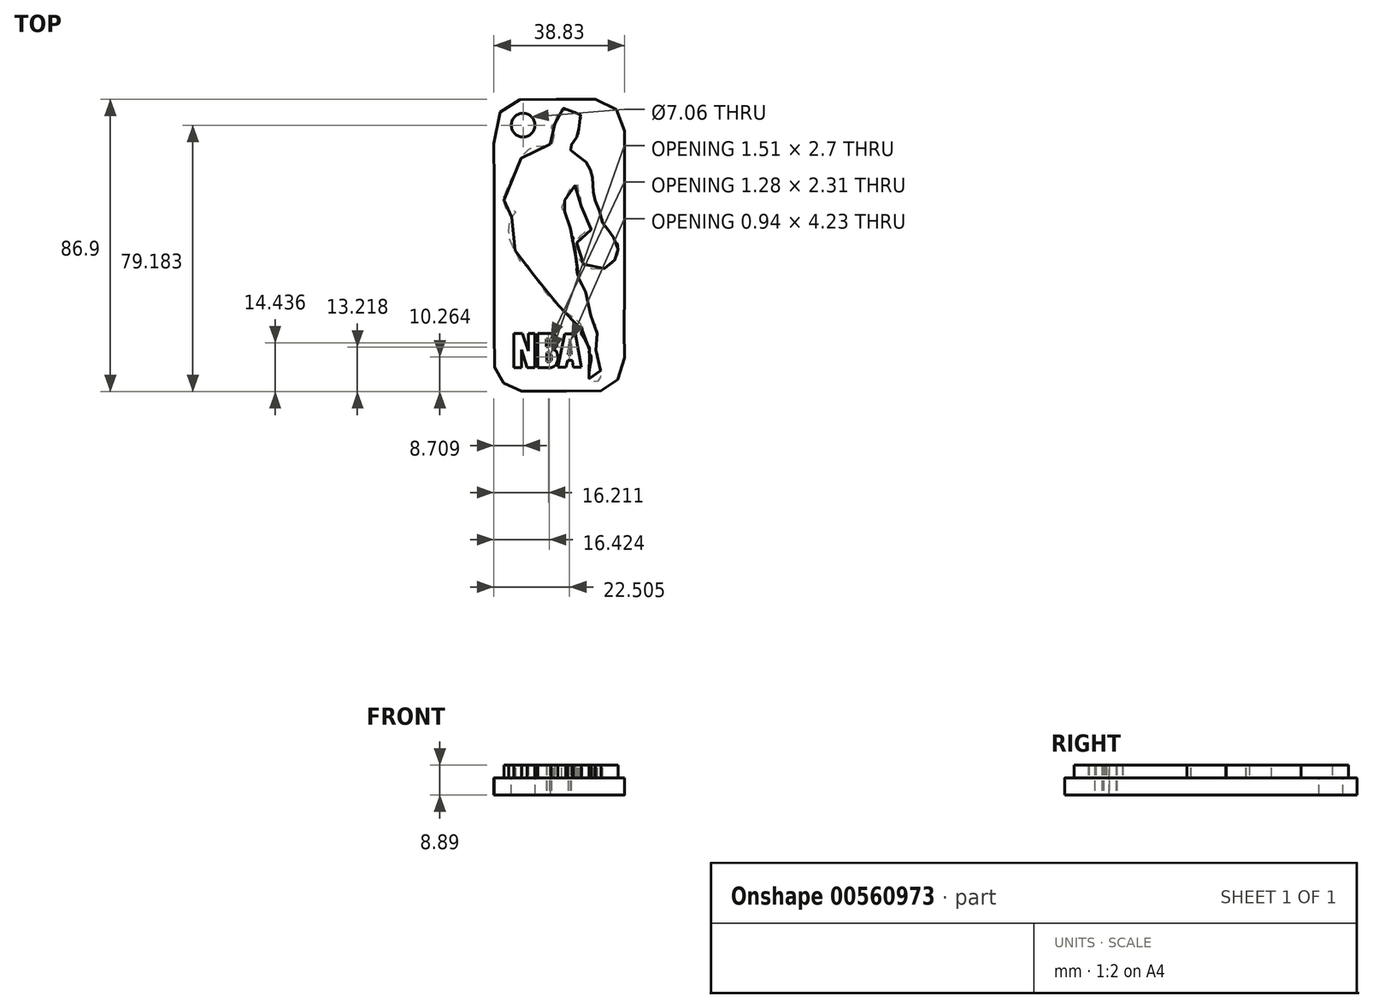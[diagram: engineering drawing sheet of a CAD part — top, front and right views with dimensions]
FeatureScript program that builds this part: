
annotation { "Feature Type Name" : "Feature", "Feature Type Description" : "" }
export const myFeature = defineFeature(function(context is Context, id is Id, definition is map)
    precondition{}
    {
        {
            var Q0;
            Q0=qCreatedBy(makeId("Top.planeOp"),FACE);
            var sketch = newSketch(context, id + "F0", { "sketchPlane" : qUnion([Q0])});
            skFitSpline(sketch, "E0", {"points": [v(-9.33, 40) * mm, v(-11.4, 39.37) * mm, v(-13.37, 38.26) * mm, v(-14.83, 36.7) * mm, v(-16.26, 34.66) * mm, v(-17.02, 30.53) * mm, v(-16.94, 24.3) * mm, v(-16.92, 18.74) * mm, v(-16.96, 10.82) * mm, v(-16.94, 3.24) * mm, v(-16.9, -4.92) * mm, v(-16.93, -14.73) * mm, v(-16.95, -25.78) * mm, v(-16.91, -36.6) * mm, v(-16.88, -38.72) * mm, v(-16.74, -39.75) * mm, v(-16.46, -40.78) * mm, v(-15.68, -42.29) * mm, v(-14.9, -43.47) * mm, v(-14.07, -44.3) * mm, v(-13.3, -45.04) * mm, v(-11.8, -45.73) * mm, v(-10.18, -46.32) * mm, v(-8.13, -46.66) * mm, v(-1.11, -46.64) * mm, v(9.32, -46.64) * mm, v(13.61, -46.6) * mm, v(14.81, -46.42) * mm, v(16.2, -45.9) * mm, v(17.42, -45.14) * mm, v(18.63, -44.28) * mm, v(19.97, -42.82) * mm, v(20.93, -41.3) * mm, v(21.45, -39.6) * mm, v(21.72, -37.14) * mm, v(21.74, -34.8) * mm, v(21.74, -34.6) * mm, v(21.7, -32.3) * mm, v(21.73, -25.46) * mm, v(21.75, -19.54) * mm, v(21.72, -12.25) * mm, v(21.74, -5.11) * mm, v(21.71, 1.16) * mm, v(21.73, 8.28) * mm, v(21.75, 14.73) * mm, v(21.75, 19.48) * mm, v(21.73, 25.05) * mm, v(21.73, 30.06) * mm, v(21.71, 32.38) * mm, v(21, 34.34) * mm, v(19.89, 36.41) * mm, v(18.65, 37.74) * mm, v(16.42, 39.18) * mm, v(14.6, 39.9) * mm, v(12.27, 40.17) * mm, v(7.1, 40.17) * mm, v(-1.12, 40.18) * mm, v(-7.54, 40.16) * mm, v(-9.33, 40) * mm]});
            skLineSegment(sketch, "E1", {"start": v(-11.06, -29.42) * mm, "end": v(-11.06, -39.6) * mm});
            skLineSegment(sketch, "E2", {"start": v(-11.06, -39.6) * mm, "end": v(-8.88, -39.6) * mm});
            skLineSegment(sketch, "E3", {"start": v(-8.88, -39.6) * mm, "end": v(-8.88, -34.23) * mm});
            skLineSegment(sketch, "E4", {"start": v(-8.88, -34.23) * mm, "end": v(-7.13, -39.6) * mm});
            skLineSegment(sketch, "E5", {"start": v(-7.13, -39.6) * mm, "end": v(-4.87, -39.6) * mm});
            skLineSegment(sketch, "E6", {"start": v(-4.87, -39.6) * mm, "end": v(-4.87, -29.4) * mm});
            skLineSegment(sketch, "E7", {"start": v(-4.87, -29.4) * mm, "end": v(-6.8, -29.4) * mm});
            skLineSegment(sketch, "E8", {"start": v(-6.8, -29.4) * mm, "end": v(-6.8, -34.66) * mm});
            skLineSegment(sketch, "E9", {"start": v(-6.8, -34.66) * mm, "end": v(-8.55, -29.4) * mm});
            skLineSegment(sketch, "E10", {"start": v(-8.55, -29.4) * mm, "end": v(-11.06, -29.42) * mm});
            skLineSegment(sketch, "E11", {"start": v(-4.06, -39.6) * mm, "end": v(-4.06, -29.42) * mm});
            skLineSegment(sketch, "E12", {"start": v(-4.06, -29.42) * mm, "end": v(0, -29.42) * mm});
            skLineSegment(sketch, "E13", {"start": v(-4.06, -39.6) * mm, "end": v(0, -39.6) * mm});
            skLineSegment(sketch, "E14", {"start": v(-1.38, -35.1) * mm, "end": v(-1.38, -37.8) * mm});
            skLineSegment(sketch, "E15", {"start": v(-1.38, -37.8) * mm, "end": v(-0.43, -37.8) * mm});
            skLineSegment(sketch, "E16", {"start": v(-1.38, -35.1) * mm, "end": v(-0.57, -35.1) * mm});
            skFitSpline(sketch, "E17", {"points": [v(-0.57, -35.1) * mm, v(0, -35.78) * mm, v(0, -37.43) * mm, v(-0.43, -37.8) * mm], "startDerivative": vector(2.1, -1.6) * mm, "endDerivative": vector(-1.94, -0.88) * mm});
            skFitSpline(sketch, "E18", {"points": [v(0, -29.42) * mm, v(0.77, -29.66) * mm, v(1.54, -30.42) * mm, v(1.8, -31.62) * mm, v(1.73, -32.67) * mm, v(1.55, -33.28) * mm, v(1.17, -33.73) * mm, v(0.76, -34.05) * mm, v(0.61, -34.18) * mm, v(1.35, -34.57) * mm, v(1.75, -35.24) * mm, v(2.02, -36.54) * mm, v(1.94, -37.43) * mm, v(1.57, -38.5) * mm, v(1.02, -39.1) * mm, v(0.1, -39.54) * mm, v(0, -39.6) * mm], "startDerivative": vector(11.98, -2.6) * mm, "endDerivative": vector(-2.87, -2.33) * mm});
            skLineSegment(sketch, "E19", {"start": v(-1.48, -31.12) * mm, "end": v(-1.48, -33.4) * mm});
            skFitSpline(sketch, "E20", {"points": [v(-1.48, -33.4) * mm, v(-0.8, -33.4) * mm, v(-0.35, -32.93) * mm, v(-0.31, -31.46) * mm, v(-0.9, -31.16) * mm, v(-1.48, -31.12) * mm], "startDerivative": vector(3.89, -0.46) * mm, "endDerivative": vector(-3.22, 0.09) * mm});
            skLineSegment(sketch, "E21", {"start": v(4.02, -29.54) * mm, "end": v(2, -39.43) * mm});
            skLineSegment(sketch, "E22", {"start": v(2, -39.43) * mm, "end": v(4.44, -39.43) * mm});
            skLineSegment(sketch, "E23", {"start": v(4.44, -39.43) * mm, "end": v(4.85, -37.43) * mm});
            skLineSegment(sketch, "E24", {"start": v(4.85, -37.43) * mm, "end": v(6.34, -37.43) * mm});
            skLineSegment(sketch, "E25", {"start": v(6.34, -37.43) * mm, "end": v(6.55, -39.43) * mm});
            skLineSegment(sketch, "E26", {"start": v(6.55, -39.43) * mm, "end": v(8.93, -39.43) * mm});
            skLineSegment(sketch, "E27", {"start": v(8.93, -39.43) * mm, "end": v(7.16, -29.54) * mm});
            skLineSegment(sketch, "E28", {"start": v(7.16, -29.54) * mm, "end": v(4.02, -29.54) * mm});
            skLineSegment(sketch, "E29", {"start": v(5.63, -31.37) * mm, "end": v(4.99, -35.6) * mm});
            skLineSegment(sketch, "E30", {"start": v(4.99, -35.6) * mm, "end": v(5.92, -35.6) * mm});
            skLineSegment(sketch, "E31", {"start": v(5.92, -35.6) * mm, "end": v(5.63, -31.37) * mm});
            skFitSpline(sketch, "E32", {"points": [v(1.08, 32.9) * mm, v(1.25, 35.17) * mm, v(2.04, 36.64) * mm, v(3.5, 37.45) * mm, v(5.98, 37.51) * mm, v(7.9, 36.13) * mm, v(8.41, 35.94) * mm, v(8.9, 34.68) * mm, v(8.88, 33.23) * mm, v(8.65, 32.2) * mm, v(8.29, 31.65) * mm, v(8.29, 31.18) * mm, v(8.48, 31.03) * mm, v(8.48, 30.67) * mm, v(8.35, 30.14) * mm, v(8.16, 29.73) * mm, v(7.95, 29.37) * mm, v(7.56, 28.92) * mm, v(7.46, 28.8) * mm, v(7.24, 28.69) * mm, v(7.11, 28.43) * mm, v(6.7, 27.84) * mm, v(6.54, 27.5) * mm, v(6.26, 27.05) * mm, v(5.98, 26.73) * mm, v(5.66, 26.4) * mm, v(5.37, 26.2) * mm, v(5.15, 26.02) * mm, v(5.15, 25.85) * mm, v(5.17, 25.5) * mm, v(5.3, 25.28) * mm, v(5.75, 25.13) * mm, v(6.1, 24.9) * mm, v(6.5, 24.55) * mm, v(6.8, 24.36) * mm, v(7.2, 24.13) * mm, v(7.4, 23.96) * mm, v(7.52, 23.55) * mm, v(7.65, 23.55) * mm, v(7.95, 23.5) * mm, v(8.18, 23.32) * mm, v(8.3, 23.2) * mm, v(8.83, 22.87) * mm, v(9.62, 22.17) * mm, v(10.28, 21.52) * mm, v(10.51, 21.27) * mm, v(10.7, 20.99) * mm, v(10.93, 20.57) * mm, v(11.16, 20.16) * mm, v(11.36, 19.79) * mm, v(11.54, 19.43) * mm, v(11.7, 19.09) * mm, v(11.82, 18.73) * mm, v(11.91, 18.48) * mm, v(12.04, 18.17) * mm, v(12.14, 17.89) * mm, v(12.2, 17.47) * mm, v(12.22, 17.17) * mm, v(12.27, 16.92) * mm, v(12.3, 16.63) * mm, v(12.36, 14.73) * mm, v(12.41, 13.66) * mm, v(12.41, 12.97) * mm, v(12.66, 12.31) * mm, v(12.68, 12.02) * mm, v(12.75, 11.6) * mm, v(12.77, 11.29) * mm, v(12.86, 10.9) * mm, v(12.92, 10.72) * mm, v(12.97, 10.28) * mm, v(13, 10.14) * mm, v(13.32, 8.74) * mm, v(13.58, 8.06) * mm, v(13.9, 7.46) * mm, v(14.16, 7.05) * mm, v(14.38, 6.77) * mm, v(14.51, 6.42) * mm, v(14.63, 6.18) * mm, v(15.07, 5.08) * mm, v(15.25, 4.3) * mm, v(15.23, 4.08) * mm, v(15.22, 3.24) * mm, v(15.3, 2.49) * mm, v(15.54, 1.88) * mm, v(15.69, 1.4) * mm, v(16.55, 1.3) * mm, v(16.96, 1.26) * mm, v(17.5, 0.71) * mm, v(17.78, 0.37) * mm, v(18, 0) * mm, v(18.12, -0.08) * mm, v(18.27, -0.27) * mm, v(18.41, -0.68) * mm, v(18.58, -0.95) * mm, v(18.73, -1.16) * mm, v(18.85, -1.33) * mm, v(18.91, -1.4) * mm, v(19.49, -2.44) * mm, v(19.82, -3.98) * mm, v(19.86, -4.87) * mm, v(19.76, -5.96) * mm, v(19.55, -6.51) * mm, v(19.24, -6.95) * mm, v(19.06, -7.22) * mm, v(18.7, -7.87) * mm, v(17.7, -8.88) * mm, v(17.2, -9.27) * mm, v(16.79, -9.51) * mm, v(16.1, -10.06) * mm, v(13.33, -10.33) * mm, v(11.13, -9.98) * mm, v(9.4, -8.7) * mm, v(7.73, -6.56) * mm, v(7.38, -3.42) * mm, v(8.1, -1.25) * mm, v(9.5, 0.33) * mm, v(11.66, 1.43) * mm, v(12, 1.39) * mm, v(11.03, 3.98) * mm, v(9, 8.27) * mm], "startDerivative": vector(0.08, 151.37) * mm, "endDerivative": vector(-87.88, 182.65) * mm});
            skFitSpline(sketch, "E33", {"points": [v(9, 8.27) * mm, v(8.7, 11.1) * mm, v(8.3, 12.3) * mm, v(8.15, 13.23) * mm, v(7.99, 13.93) * mm, v(7.91, 14.8) * mm, v(7.16, 14.53) * mm, v(6.35, 14.06) * mm, v(5.4, 13.47) * mm, v(5.06, 12.62) * mm, v(4.87, 12.3) * mm, v(4.74, 11.78) * mm, v(4.63, 11.5) * mm, v(4.22, 10.55) * mm, v(4.04, 10.22) * mm, v(3.77, 9.61) * mm, v(3.56, 9.13) * mm, v(3.29, 8.6) * mm, v(3.16, 8.27) * mm, v(3.16, 7.91) * mm, v(3.16, 7.73) * mm, v(3.29, 7.52) * mm, v(3.54, 7.37) * mm, v(3.83, 7.25) * mm, v(3.97, 6.9) * mm, v(4.04, 6.73) * mm, v(4.19, 6.46) * mm, v(4.26, 6.28) * mm, v(4.92, 4.67) * mm, v(4.96, 3.88) * mm, v(5.15, 3.59) * mm, v(5.31, 3.24) * mm, v(5.33, 3.05) * mm, v(5.46, 2.53) * mm, v(5.6, 2.07) * mm, v(5.73, 1.5) * mm, v(5.83, 1.13) * mm, v(5.96, 0.7) * mm, v(6.1, 0.3) * mm, v(6.18, 0) * mm, v(6.25, -0.21) * mm, v(6.43, -0.73) * mm, v(6.5, -1) * mm, v(6.57, -1.3) * mm, v(6.57, -1.36) * mm, v(6.35, -1.6) * mm, v(6.8, -3.46) * mm, v(6.93, -3.97) * mm, v(6.98, -4.39) * mm, v(7.04, -5.09) * mm, v(7.14, -5.59) * mm, v(7.18, -5.9) * mm, v(7.3, -6.32) * mm, v(7.3, -6.65) * mm, v(7.38, -7.3) * mm, v(7.48, -7.85) * mm, v(7.5, -8.22) * mm, v(7.63, -9.84) * mm, v(7.6, -10.12) * mm, v(7.72, -11.3) * mm, v(7.84, -11.83) * mm, v(8.04, -12.47) * mm, v(8.24, -13.05) * mm, v(8.33, -13.37) * mm, v(8.54, -13.83) * mm, v(8.65, -14.12) * mm, v(9, -14.52) * mm, v(9, -14.86) * mm, v(9.26, -15.18) * mm, v(9.44, -15.56) * mm, v(9.76, -16.15) * mm, v(9.92, -16.5) * mm, v(10.48, -18.04) * mm, v(10.54, -18.35) * mm, v(10.81, -19.39) * mm, v(11.05, -20.27) * mm, v(11.22, -21.3) * mm, v(11.67, -23.41) * mm, v(11.8, -24.24) * mm, v(12.03, -25.17) * mm, v(12.36, -26.02) * mm, v(12.83, -26.71) * mm, v(13.36, -27.37) * mm, v(13.57, -27.87) * mm, v(13.74, -28.38) * mm, v(13.77, -29.1) * mm, v(13.4, -30.48) * mm, v(13.24, -31.05) * mm, v(13.18, -31.43) * mm, v(13.09, -32) * mm, v(13.07, -32.26) * mm, v(13.18, -32.8) * mm, v(13.18, -33.45) * mm, v(13.15, -33.75) * mm, v(13.25, -34.28) * mm, v(13.54, -34.97) * mm, v(13.87, -36.15) * mm, v(14.05, -36.31) * mm, v(14.23, -38.29) * mm, v(14.32, -38.64) * mm, v(14.52, -39.5) * mm, v(14.58, -40.13) * mm, v(14.78, -41.42) * mm, v(14.72, -41.83) * mm, v(14.49, -42.93) * mm, v(13.98, -43.6) * mm, v(12.68, -43.91) * mm, v(12.32, -43.82) * mm, v(11.5, -43.38) * mm, v(11.58, -38.9) * mm, v(11.9, -36.13) * mm, v(11.57, -35.7) * mm, v(11.28, -35.36) * mm, v(11.23, -34.9) * mm, v(11.34, -34.54) * mm, v(11.35, -34.22) * mm, v(11.34, -33.66) * mm, v(11.22, -33.46) * mm, v(11.1, -33.31) * mm, v(10.87, -32.98) * mm, v(9.92, -30.96) * mm, v(9, -29.73) * mm, v(9, -28.76) * mm, v(9.32, -28.19) * mm, v(8.8, -27.13) * mm, v(8.52, -26.27) * mm, v(6.36, -24.7) * mm, v(2.17, -21.07) * mm, v(0.64, -19.73) * mm, v(-1.17, -17.7) * mm, v(-2.4, -16.08) * mm, v(-5.4, -11.73) * mm, v(-7, -9.12) * mm, v(-7.13, -9.12) * mm, v(-8.75, -8.9) * mm, v(-9.03, -8.47) * mm, v(-10.5, -5.23) * mm, v(-11.78, -2.86) * mm, v(-12.63, -0.18) * mm, v(-12.45, 2.66) * mm, v(-12, 4.87) * mm, v(-10.7, 6.23) * mm, v(-10.55, 7.15) * mm, v(-12.98, 7.25) * mm, v(-13.49, 7.78) * mm, v(-13.95, 9.23) * mm, v(-13.95, 10.95) * mm, v(-12.53, 14.8) * mm, v(-10.4, 19.11) * mm, v(-8.75, 23.02) * mm, v(-7.18, 24.82) * mm, v(-5.58, 25.88) * mm, v(-2.28, 26.34) * mm, v(-0.43, 26.74) * mm, v(0.28, 27.05) * mm, v(0.68, 28.21) * mm, v(0.94, 29.99) * mm, v(0.33, 30.8) * mm, v(0.2, 32.42) * mm, v(1.08, 32.9) * mm], "startDerivative": vector(-15.98, 279.85) * mm, "endDerivative": vector(159.3, 38.13) * mm});
            skSolve(sketch);
        }
        {
            var Q0;
            Q0=makeQuery(id+"F0.imprint","IMPRINT",FACE,{"disambiguationData":[TD([[makeQuery(id+"F0.imprint","IMPRINT",EDGE,{"derivedFrom":sQuery(id+"F0.wireOp",EDGE,"E0")}),1.0]])]});
            extrude(context, id + "F1", {"entities" : qUnion([Q0]), "depth" : 5.08 * mm, "offsetDistance" : 25.4 * mm});
        }
        {
            var Q0;
            Q0=makeQuery(id+"F0.imprint","IMPRINT",FACE,{"disambiguationData":[TD([[makeQuery(id+"F0.imprint","IMPRINT",EDGE,{"derivedFrom":sQuery(id+"F0.wireOp",EDGE,"E32")}),-1.0]])]});
            var Q1;
            Q1=makeQuery(id+"F0.imprint","IMPRINT",FACE,{"disambiguationData":[TD([[makeQuery(id+"F0.imprint","IMPRINT",EDGE,{"derivedFrom":sQuery(id+"F0.wireOp",EDGE,"E1")}),1.0]])]});
            var Q2;
            Q2=makeQuery(id+"F0.imprint","IMPRINT",FACE,{"disambiguationData":[TD([[makeQuery(id+"F0.imprint","IMPRINT",EDGE,{"derivedFrom":sQuery(id+"F0.wireOp",EDGE,"E11")}),-1.0]])]});
            var Q3;
            Q3=makeQuery(id+"F0.imprint","IMPRINT",FACE,{"disambiguationData":[TD([[makeQuery(id+"F0.imprint","IMPRINT",EDGE,{"derivedFrom":sQuery(id+"F0.wireOp",EDGE,"E21")}),1.0]])]});
            extrude(context, id + "F2", {"entities" : qUnion([Q0, Q1, Q2, Q3]), "operationType" : NewBodyOperationType.ADD, "depth" : 8.9 * mm, "offsetDistance" : 25.4 * mm});
        }
        {
            var Q0;
            Q0=makeQuery(id+"F1.opExtrude","CAP_FACE",FACE,{"disambiguationData":[OSD([sQuery(id+"F0.wireOp",EDGE,"E0"),sQuery(id+"F0.wireOp",EDGE,"E1"),sQuery(id+"F0.wireOp",EDGE,"E2"),sQuery(id+"F0.wireOp",EDGE,"E3"),sQuery(id+"F0.wireOp",EDGE,"E4"),sQuery(id+"F0.wireOp",EDGE,"E5"),sQuery(id+"F0.wireOp",EDGE,"E6"),sQuery(id+"F0.wireOp",EDGE,"E7"),sQuery(id+"F0.wireOp",EDGE,"E8"),sQuery(id+"F0.wireOp",EDGE,"E9"),sQuery(id+"F0.wireOp",EDGE,"E10"),sQuery(id+"F0.wireOp",EDGE,"E11"),sQuery(id+"F0.wireOp",EDGE,"E12"),sQuery(id+"F0.wireOp",EDGE,"E13"),sQuery(id+"F0.wireOp",EDGE,"E18"),sQuery(id+"F0.wireOp",EDGE,"E21"),sQuery(id+"F0.wireOp",EDGE,"E22"),sQuery(id+"F0.wireOp",EDGE,"E23"),sQuery(id+"F0.wireOp",EDGE,"E24"),sQuery(id+"F0.wireOp",EDGE,"E25"),sQuery(id+"F0.wireOp",EDGE,"E26"),sQuery(id+"F0.wireOp",EDGE,"E27"),sQuery(id+"F0.wireOp",EDGE,"E28"),sQuery(id+"F0.wireOp",EDGE,"E32"),sQuery(id+"F0.wireOp",EDGE,"E33")])],"isStart":false});
            var sketch = newSketch(context, id + "F3", { "sketchPlane" : qUnion([Q0])});
            skCircle(sketch, "E34", {"center": v(-8.34, 32.47) * mm, "radius": 3.53 * mm});
            skSolve(sketch);
        }
        {
            var Q0;
            Q0=makeQuery(id+"F3.imprint","IMPRINT",FACE,{"disambiguationData":[TD([[makeQuery(id+"F3.imprint","IMPRINT",EDGE,{"derivedFrom":sQuery(id+"F3.wireOp",EDGE,"E34")}),1.0]])]});
            extrude(context, id + "F4", {"entities" : qUnion([Q0]), "operationType" : NewBodyOperationType.REMOVE, "oppositeDirection" : true, "depth" : 25.4 * mm, "offsetDistance" : 25.4 * mm});
        }
    });
